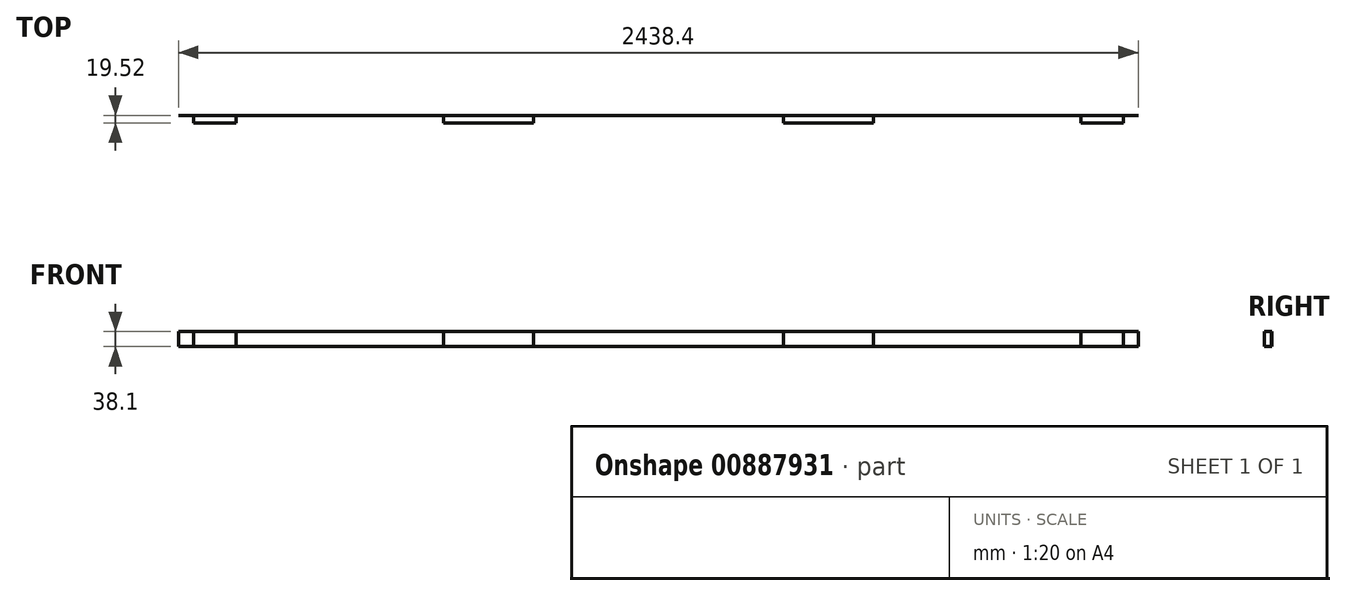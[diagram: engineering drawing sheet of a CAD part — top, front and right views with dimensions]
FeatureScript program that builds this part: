
annotation { "Feature Type Name" : "Feature", "Feature Type Description" : "" }
export const myFeature = defineFeature(function(context is Context, id is Id, definition is map)
    precondition{}
    {
        {
            assignVariable(context, id + "F0", {"name" : "WoodThickness", "anyValue" : .47});
        }
        {
            var Q0;
            Q0=qCreatedBy(makeId("Front.planeOp"),FACE);
            var sketch = newSketch(context, id + "F1", { "sketchPlane" : qUnion([Q0])});
            skLineSegment(sketch, "E0.bottom", {"start": v(0, 0) * mm, "end": v(2438.4, 0) * mm});
            skLineSegment(sketch, "E0.top", {"start": v(0, -38.1) * mm, "end": v(2438.4, -38.1) * mm});
            skLineSegment(sketch, "E0.left", {"start": v(0, 0) * mm, "end": v(0, -38.1) * mm});
            skLineSegment(sketch, "E0.right", {"start": v(2438.4, 0) * mm, "end": v(2438.4, -38.1) * mm});
            skSolve(sketch);
        }
        {
            var Q0;
            Q0 = qSketchRegion(id + "F1", true);
            extrude(context, id + "F2", {"entities" : qUnion([Q0]), "depth" : (getVariable(context, 'WoodThickness')) * mm, "offsetDistance" : 25.4 * mm});
        }
        {
            var Q0;
            Q0=makeQuery(id+"F2.opExtrude","CAP_FACE",FACE,{"disambiguationData":[OSD([sQuery(id+"F1.wireOp",EDGE,"E0.bottom"),sQuery(id+"F1.wireOp",EDGE,"E0.top"),sQuery(id+"F1.wireOp",EDGE,"E0.left"),sQuery(id+"F1.wireOp",EDGE,"E0.right")])],"isStart":false});
            var sketch = newSketch(context, id + "F3", { "sketchPlane" : qUnion([Q0])});
            skLineSegment(sketch, "E1", {"start": v(1219.2, 0) * mm, "end": v(1219.2, -38.1) * mm, "construction": true});
            skLineSegment(sketch, "E2.bottom", {"start": v(38.1, -38.1) * mm, "end": v(146.05, -38.1) * mm});
            skLineSegment(sketch, "E2.top", {"start": v(38.1, 0) * mm, "end": v(146.05, 0) * mm});
            skLineSegment(sketch, "E2.left", {"start": v(38.1, -38.1) * mm, "end": v(38.1, 0) * mm});
            skLineSegment(sketch, "E2.right", {"start": v(146.05, -38.1) * mm, "end": v(146.05, 0) * mm});
            skLineSegment(sketch, "E3.MirrorCS", {"start": v(2292.35, -38.1) * mm, "end": v(2292.35, 0) * mm});
            skLineSegment(sketch, "E4.MirrorCS", {"start": v(2400.3, 0) * mm, "end": v(2292.35, 0) * mm});
            skLineSegment(sketch, "E5.MirrorCS", {"start": v(2400.3, -38.1) * mm, "end": v(2400.3, 0) * mm});
            skLineSegment(sketch, "E6.MirrorCS", {"start": v(2400.3, -38.1) * mm, "end": v(2292.35, -38.1) * mm});
            skLineSegment(sketch, "E7.bottom", {"start": v(673.1, 0) * mm, "end": v(901.7, 0) * mm});
            skLineSegment(sketch, "E7.top", {"start": v(673.1, -38.1) * mm, "end": v(901.7, -38.1) * mm});
            skLineSegment(sketch, "E7.left", {"start": v(673.1, 0) * mm, "end": v(673.1, -38.1) * mm});
            skLineSegment(sketch, "E7.right", {"start": v(901.7, 0) * mm, "end": v(901.7, -38.1) * mm});
            skLineSegment(sketch, "E8.bottom", {"start": v(1536.7, 0) * mm, "end": v(1765.3, 0) * mm});
            skLineSegment(sketch, "E8.top", {"start": v(1536.7, -38.1) * mm, "end": v(1765.3, -38.1) * mm});
            skLineSegment(sketch, "E8.left", {"start": v(1536.7, 0) * mm, "end": v(1536.7, -38.1) * mm});
            skLineSegment(sketch, "E8.right", {"start": v(1765.3, 0) * mm, "end": v(1765.3, -38.1) * mm});
            skLineSegment(sketch, "E9", {"start": v(901.7, 0) * mm, "end": v(1219.2, 0) * mm, "construction": true});
            skLineSegment(sketch, "E10", {"start": v(1219.2, 0) * mm, "end": v(1536.7, 0) * mm, "construction": true});
            skSolve(sketch);
        }
        {
            var Q0;
            Q0 = qSketchRegion(id + "F3", true);
            extrude(context, id + "F4", {"entities" : qUnion([Q0]), "operationType" : NewBodyOperationType.ADD, "depth" : 19.05 * mm, "offsetDistance" : 25.4 * mm});
        }
    });
